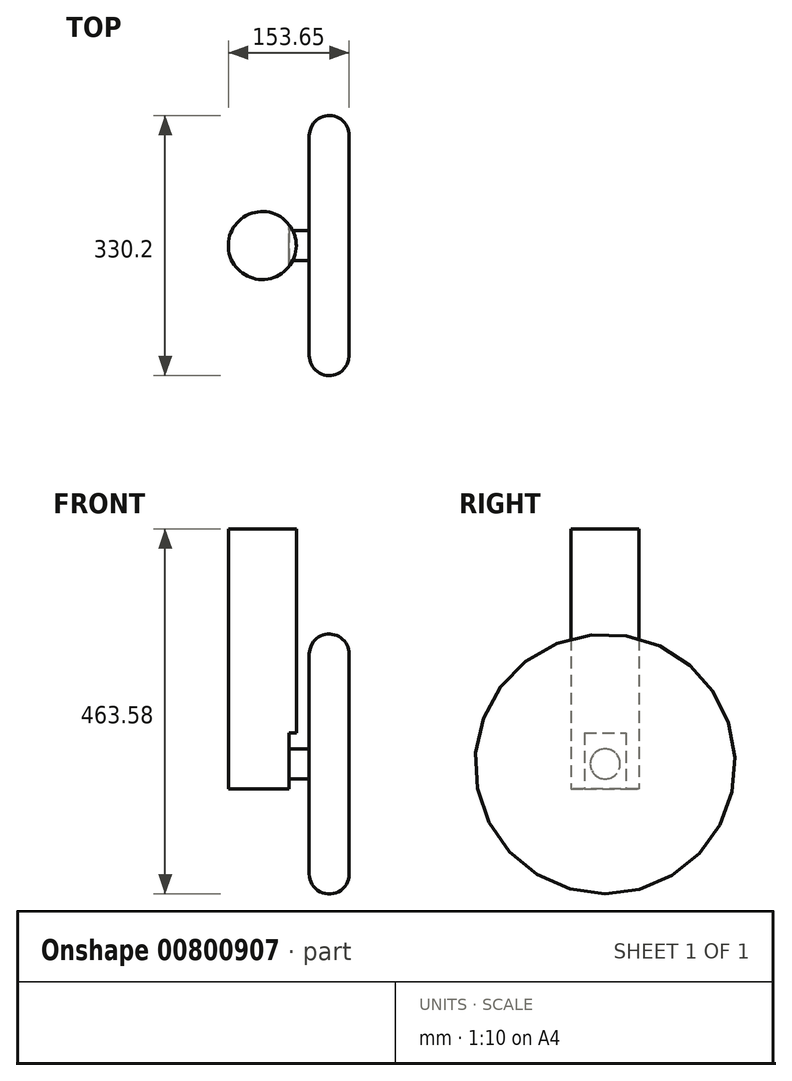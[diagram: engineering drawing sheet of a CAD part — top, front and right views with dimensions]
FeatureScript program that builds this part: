
annotation { "Feature Type Name" : "Feature", "Feature Type Description" : "" }
export const myFeature = defineFeature(function(context is Context, id is Id, definition is map)
    precondition{}
    {
        {
            var Q0;
            Q0=qCreatedBy(makeId("Top.planeOp"),FACE);
            var sketch = newSketch(context, id + "F0", { "sketchPlane" : qUnion([Q0])});
            skCircle(sketch, "E0", {"center": v(0, 0) * mm, "radius": 43.18 * mm});
            skSolve(sketch);
        }
        {
            var Q0;
            Q0=makeQuery(id+"F0.imprint","IMPRINT",FACE,{"disambiguationData":[TD([[makeQuery(id+"F0.imprint","IMPRINT",EDGE,{"derivedFrom":sQuery(id+"F0.wireOp",EDGE,"E0")}),1.0]])]});
            extrude(context, id + "F1", {"entities" : qUnion([Q0]), "depth" : 330.2 * mm, "offsetDistance" : 25.4 * mm});
        }
        {
            var Q0;
            Q0=makeQuery(id+"F1.opExtrude","CAP_FACE",FACE,{"disambiguationData":[OSD([sQuery(id+"F0.wireOp",EDGE,"E0")])],"isStart":true});
            var sketch = newSketch(context, id + "F2", { "sketchPlane" : qUnion([Q0])});
            skLineSegment(sketch, "E1", {"start": v(34.27, 26.27) * mm, "end": v(34.27, -26.27) * mm});
            skSolve(sketch);
        }
        {
            var Q0;
            {var subQ0=sQuery(id+"F2.wireOp",EDGE,"E1");Q0=makeQuery(id+"F2.imprint","IMPRINT",FACE,{"disambiguationData":[TD([[makeQuery(id+"F2.imprint","IMPRINT",EDGE,{"derivedFrom":subQ0}),1.0]])]});}
            extrude(context, id + "F3", {"entities" : qUnion([Q0]), "operationType" : NewBodyOperationType.REMOVE, "oppositeDirection" : true, "depth" : 71.12 * mm, "offsetDistance" : 25.4 * mm});
        }
        {
            var Q0;
            Q0=makeQuery(id+"F3.boolean.opBoolean","COPY",FACE,{"derivedFrom":makeQuery(id+"F3.opExtrude","SWEPT_FACE",FACE,{"disambiguationData":[OSD([sQuery(id+"F2.wireOp",EDGE,"E1")])]})});
            var sketch = newSketch(context, id + "F4", { "sketchPlane" : qUnion([Q0])});
            skCircle(sketch, "E2", {"center": v(0, 31.72) * mm, "radius": 19.05 * mm});
            skSolve(sketch);
        }
        {
            var Q0;
            Q0 = qSketchRegion(id + "F4", true);
            extrude(context, id + "F5", {"entities" : qUnion([Q0]), "operationType" : NewBodyOperationType.ADD, "depth" : 76.2 * mm, "offsetDistance" : 25.4 * mm});
        }
        {
            var Q0;
            Q0=makeQuery(id+"F5.opExtrude","CAP_FACE",FACE,{"disambiguationData":[OSD([sQuery(id+"F4.wireOp",EDGE,"E2")])],"isStart":false});
            var sketch = newSketch(context, id + "F6", { "sketchPlane" : qUnion([Q0])});
            skCircle(sketch, "E3", {"center": v(0, 31.72) * mm, "radius": 165.1 * mm});
            skSolve(sketch);
        }
        {
            var Q0;
            Q0=makeQuery(id+"F6.imprint","IMPRINT",FACE,{"disambiguationData":[TD([[makeQuery(id+"F6.imprint","IMPRINT",EDGE,{"derivedFrom":sQuery(id+"F6.wireOp",EDGE,"E3")}),1.0]])]});
            extrude(context, id + "F7", {"entities" : qUnion([Q0]), "operationType" : NewBodyOperationType.ADD, "oppositeDirection" : true, "depth" : 50.8 * mm, "offsetDistance" : 25.4 * mm});
        }
        {
            var Q0;
            Q0=makeQuery(id+"F7.opExtrude","CAP_EDGE",EDGE,{"disambiguationData":[OSD([sQuery(id+"F6.wireOp",EDGE,"E3")])],"isStart":true});
            var Q1;
            Q1=makeQuery(id+"F7.opExtrude","CAP_EDGE",EDGE,{"disambiguationData":[OSD([sQuery(id+"F6.wireOp",EDGE,"E3")])],"isStart":false});
            fillet(context, id + "F8", {"entities" : qUnion([Q0, Q1]), "radius" : 25.4 * mm, "tangentPropagation" : true, "allowEdgeOverflow" : false});
        }
    });
